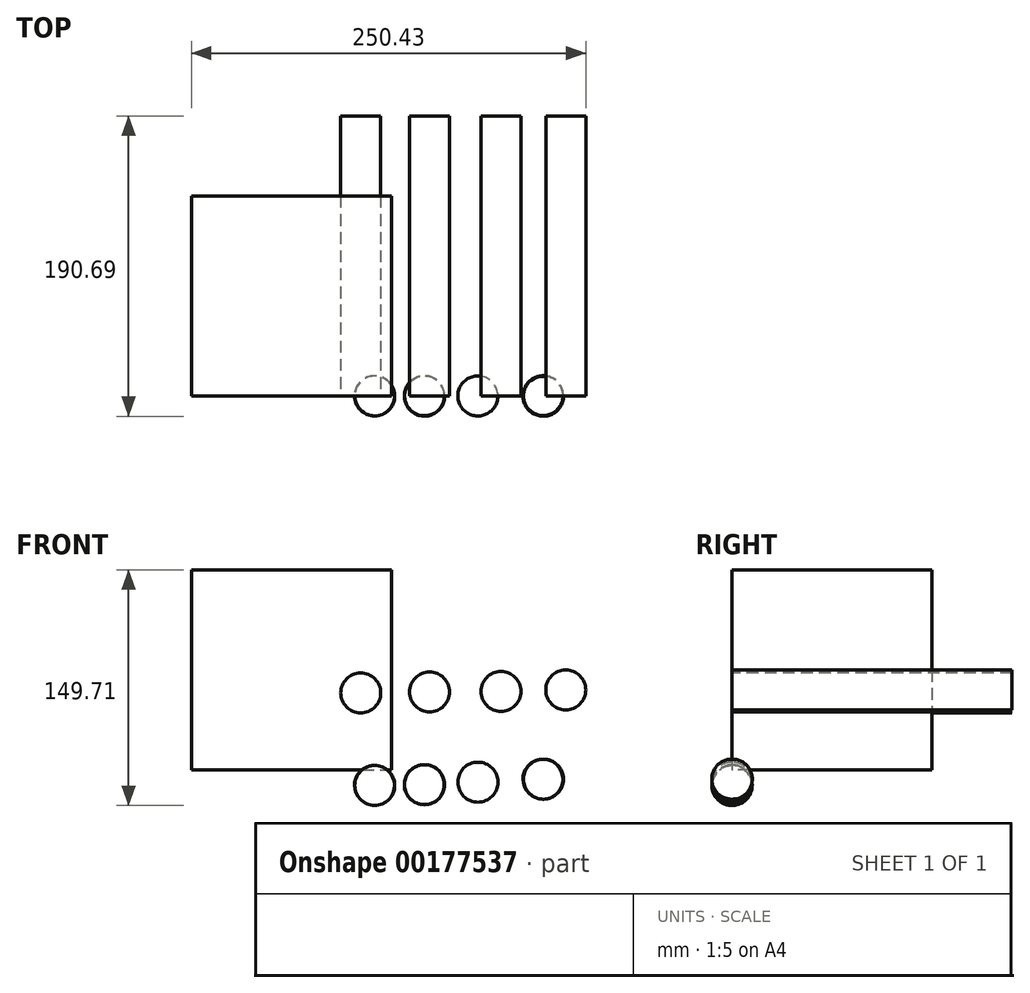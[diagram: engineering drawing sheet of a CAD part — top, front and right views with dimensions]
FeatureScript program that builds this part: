
annotation { "Feature Type Name" : "Feature", "Feature Type Description" : "" }
export const myFeature = defineFeature(function(context is Context, id is Id, definition is map)
    precondition{}
    {
        {
            var Q0;
            Q0=qCreatedBy(makeId("Front.planeOp"),FACE);
            var sketch = newSketch(context, id + "F0", { "sketchPlane" : qUnion([Q0])});
            skLineSegment(sketch, "E0.bottom", {"start": v(-31.13, 90.1) * mm, "end": v(95.87, 90.1) * mm});
            skLineSegment(sketch, "E0.top", {"start": v(-31.13, -36.9) * mm, "end": v(95.87, -36.9) * mm});
            skLineSegment(sketch, "E0.left", {"start": v(-31.13, 90.1) * mm, "end": v(-31.13, -36.9) * mm});
            skLineSegment(sketch, "E0.right", {"start": v(95.87, 90.1) * mm, "end": v(95.87, -36.9) * mm});
            skSolve(sketch);
        }
        {
            var Q0;
            Q0=qSketchRegion(id+"F0",true);
            extrude(context, id + "F1", {"entities" : qUnion([Q0]), "oppositeDirection" : true, "depth" : 127 * mm});
        }
        {
            var Q0;
            Q0=qCreatedBy(makeId("Front.planeOp"),FACE);
            var sketch = newSketch(context, id + "F2", { "sketchPlane" : qUnion([Q0])});
            skCircle(sketch, "E1", {"center": v(76.37, 11.88) * mm, "radius": 12.7 * mm});
            skCircle(sketch, "E2", {"center": v(120.1, 12.52) * mm, "radius": 12.7 * mm});
            skCircle(sketch, "E3", {"center": v(165.4, 12.83) * mm, "radius": 12.7 * mm});
            skCircle(sketch, "E4", {"center": v(206.6, 13.78) * mm, "radius": 12.7 * mm});
            skSolve(sketch);
        }
        {
            var Q0;
            Q0=qSketchRegion(id+"F2",true);
            extrude(context, id + "F3", {"entities" : qUnion([Q0]), "oppositeDirection" : true, "depth" : 177.8 * mm});
        }
        {
            var Q0;
            Q0=qCreatedBy(makeId("Front.planeOp"),FACE);
            var sketch = newSketch(context, id + "F4", { "sketchPlane" : qUnion([Q0])});
            skLineSegment(sketch, "E5", {"start": v(85.18, -34.2) * mm, "end": v(85.18, -59.6) * mm});
            skLineSegment(sketch, "E6", {"start": v(116.86, -33.7) * mm, "end": v(116.86, -59.1) * mm});
            skLineSegment(sketch, "E7", {"start": v(150.77, -32.11) * mm, "end": v(150.77, -57.51) * mm});
            skLineSegment(sketch, "E8", {"start": v(192.28, -30.21) * mm, "end": v(192.28, -55.61) * mm});
            skArc(sketch, "E9", {"start": v(85.18, -34.2) * mm, "mid": v(72.39, -46.9) * mm, "end": v(85.18, -59.6) * mm});
            skArc(sketch, "E10", {"start": v(116.86, -33.7) * mm, "mid": v(104.05, -46.4) * mm, "end": v(116.86, -59.1) * mm});
            skArc(sketch, "E11", {"start": v(150.77, -32.11) * mm, "mid": v(138.07, -44.81) * mm, "end": v(150.77, -57.51) * mm});
            skArc(sketch, "E12", {"start": v(192.28, -30.21) * mm, "mid": v(179.76, -42.91) * mm, "end": v(192.28, -55.61) * mm});
            skSolve(sketch);
        }
        {
            var Q0;
            Q0=makeQuery(id+"F4.imprint","IMPRINT",FACE,{"disambiguationData":[TD([[makeQuery(id+"F4.imprint","IMPRINT",EDGE,{"derivedFrom":sQuery(id+"F4.wireOp",EDGE,"E5")}),-1.0]])]});
            var Q1;
            Q1=sQuery(id+"F4.wireOp",EDGE,"E5");
            revolve(context, id + "F5", {"entities" : qUnion([Q0]), "axis" : qUnion([Q1]), "revolveType" : RevolveType.FULL});
        }
        {
            var Q0;
            Q0=makeQuery(id+"F4.imprint","IMPRINT",FACE,{"disambiguationData":[TD([[makeQuery(id+"F4.imprint","IMPRINT",EDGE,{"derivedFrom":sQuery(id+"F4.wireOp",EDGE,"E6")}),-1.0]])]});
            var Q1;
            Q1=sQuery(id+"F4.wireOp",EDGE,"E6");
            revolve(context, id + "F6", {"entities" : qUnion([Q0]), "axis" : qUnion([Q1]), "revolveType" : RevolveType.FULL});
        }
        {
            var Q0;
            Q0=makeQuery(id+"F4.imprint","IMPRINT",FACE,{"disambiguationData":[TD([[makeQuery(id+"F4.imprint","IMPRINT",EDGE,{"derivedFrom":sQuery(id+"F4.wireOp",EDGE,"E7")}),-1.0]])]});
            var Q1;
            Q1=sQuery(id+"F4.wireOp",EDGE,"E7");
            revolve(context, id + "F7", {"entities" : qUnion([Q0]), "axis" : qUnion([Q1]), "revolveType" : RevolveType.FULL});
        }
        {
            var Q0;
            Q0=makeQuery(id+"F4.imprint","IMPRINT",FACE,{"disambiguationData":[TD([[makeQuery(id+"F4.imprint","IMPRINT",EDGE,{"derivedFrom":sQuery(id+"F4.wireOp",EDGE,"E8")}),-1.0]])]});
            var Q1;
            Q1=sQuery(id+"F4.wireOp",EDGE,"E8");
            revolve(context, id + "F8", {"entities" : qUnion([Q0]), "axis" : qUnion([Q1]), "revolveType" : RevolveType.FULL});
        }
    });
